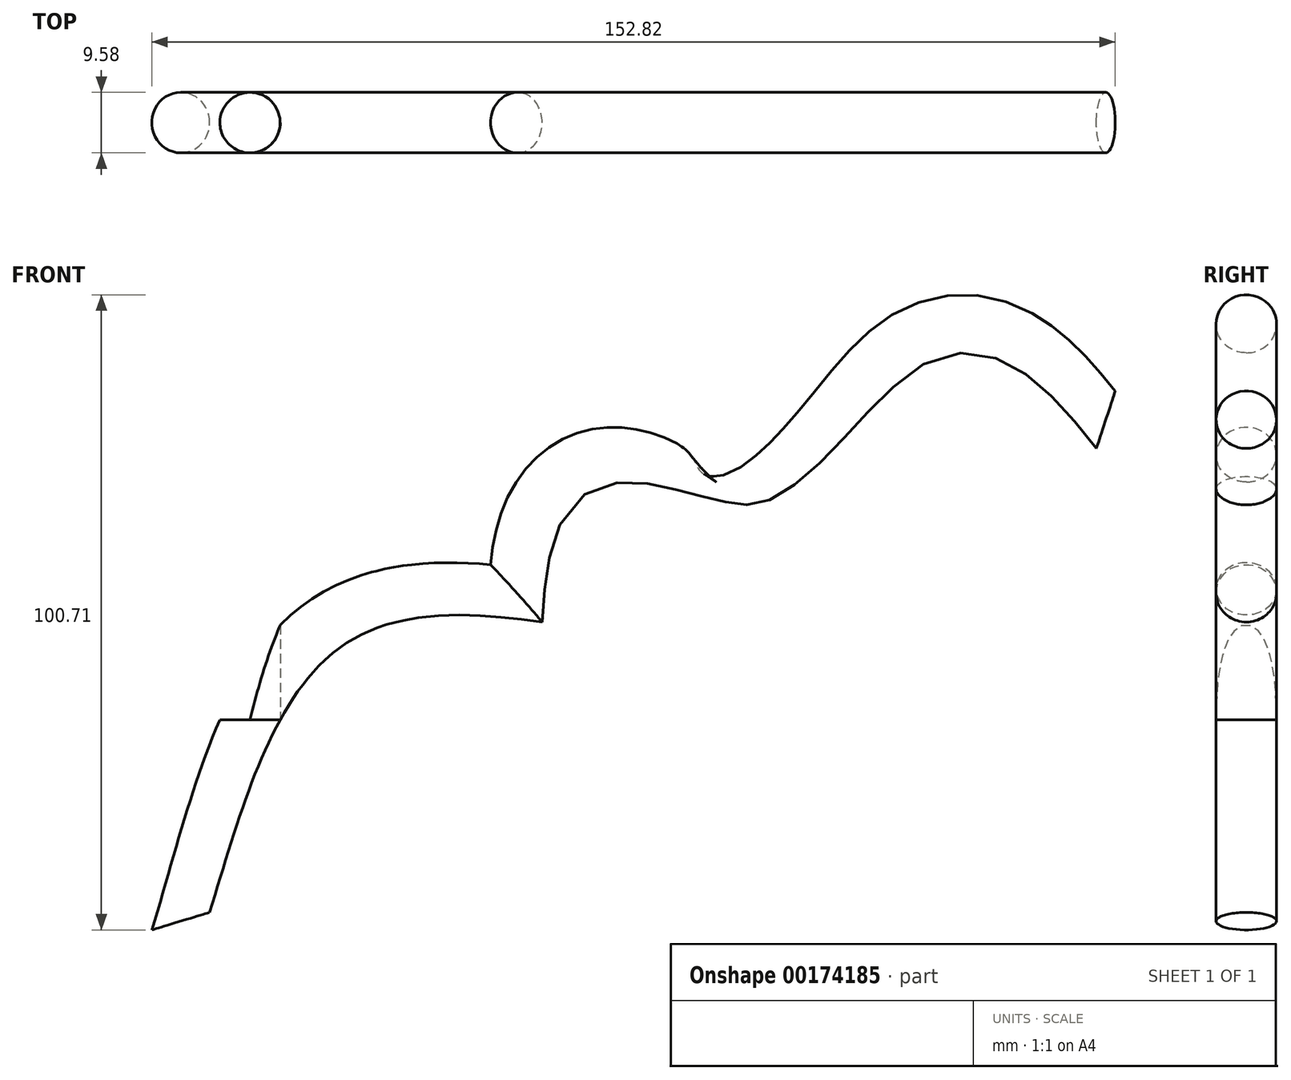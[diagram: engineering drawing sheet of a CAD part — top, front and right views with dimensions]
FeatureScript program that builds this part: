
annotation { "Feature Type Name" : "Feature", "Feature Type Description" : "" }
export const myFeature = defineFeature(function(context is Context, id is Id, definition is map)
    precondition{}
    {
        {
            var Q0;
            Q0=qCreatedBy(makeId("Front.planeOp"),FACE);
            var sketch = newSketch(context, id + "F0", { "sketchPlane" : qUnion([Q0])});
            skFitSpline(sketch, "E0", {"points": [v(-62.77, -28.6) * mm, v(-44.29, 7.19) * mm, v(-11.15, 8.95) * mm], "startDerivative": vector(26.24, 85.19) * mm, "endDerivative": vector(77.83, -11.66) * mm});
            skFitSpline(sketch, "E1", {"points": [v(-11.15, 8.95) * mm, v(-4.99, 31.24) * mm, v(20.82, 29.77) * mm, v(48.98, 51.77) * mm, v(69.22, 36.52) * mm], "startDerivative": vector(5.94, 131.4) * mm, "endDerivative": vector(82.46, -105.9) * mm});
            skSolve(sketch);
        }
        {
            var Q0;
            Q0=qCreatedBy(makeId("Top.planeOp"),FACE);
            var sketch = newSketch(context, id + "F1", { "sketchPlane" : qUnion([Q0])});
            skCircle(sketch, "E2", {"center": v(-62.89, 0) * mm, "radius": 4.79 * mm});
            skSolve(sketch);
        }
        {
            var Q0;
            Q0=makeQuery(id+"F1.imprint","IMPRINT",FACE,{"disambiguationData":[TD([[makeQuery(id+"F1.imprint","IMPRINT",EDGE,{"derivedFrom":sQuery(id+"F1.wireOp",EDGE,"E2")}),1.0]])]});
            var sketch = newSketch(context, id + "F2", { "sketchPlane" : qUnion([Q0])});
            skSolve(sketch);
        }
        {
            var Q0;
            Q0=makeQuery(id+"F1.imprint","IMPRINT",FACE,{"disambiguationData":[TD([[makeQuery(id+"F1.imprint","IMPRINT",EDGE,{"derivedFrom":sQuery(id+"F1.wireOp",EDGE,"E2")}),1.0]])]});
            var Q1;
            Q1=sQuery(id+"F0.wireOp",EDGE,"E0");
            var Q2;
            Q2=sQuery(id+"F0.wireOp",EDGE,"E1");
            sweep(context, id + "F3", {"profiles" : qUnion([Q0]), "path" : qUnion([Q1, Q2])});
        }
        {
            var Q0;
            Q0=makeQuery(id+"F2.imprint","IMPRINT",FACE,{"disambiguationData":[TD([[makeQuery(id+"F2.imprint","IMPRINT",EDGE,{"derivedFrom":makeQuery(id+"F1.imprint","IMPRINT",EDGE,{"derivedFrom":sQuery(id+"F1.wireOp",EDGE,"E2")})}),1.0]])]});
            extrude(context, id + "F4", {"entities" : qUnion([Q0]), "operationType" : NewBodyOperationType.REMOVE, "depth" : 271.9 * mm});
        }
    });
